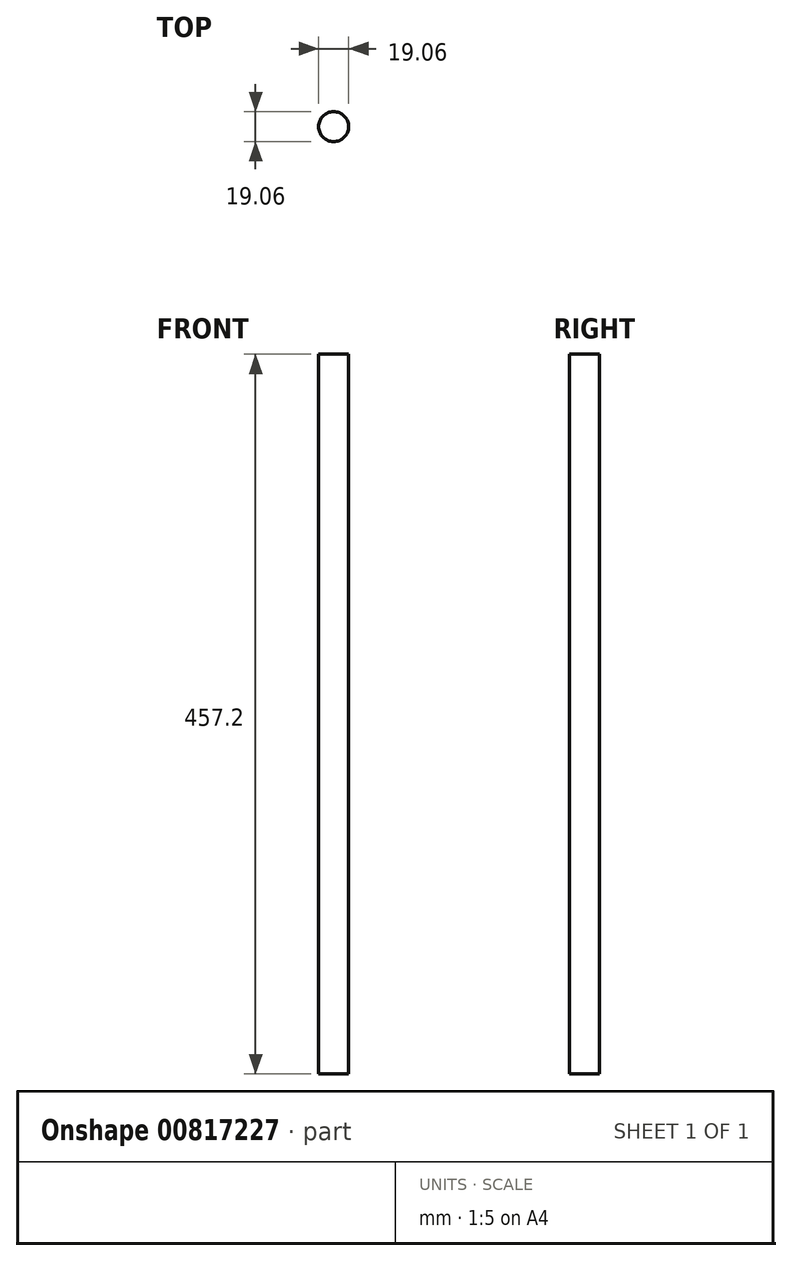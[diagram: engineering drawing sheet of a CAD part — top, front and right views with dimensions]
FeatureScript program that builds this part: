
annotation { "Feature Type Name" : "Feature", "Feature Type Description" : "" }
export const myFeature = defineFeature(function(context is Context, id is Id, definition is map)
    precondition{}
    {
        {
            var Q0;
            Q0=qCreatedBy(makeId("Top.planeOp"),FACE);
            var sketch = newSketch(context, id + "F0", { "sketchPlane" : qUnion([Q0])});
            skCircle(sketch, "E0", {"center": v(0, 0) * mm, "radius": 9.53 * mm});
            skSolve(sketch);
        }
        {
            var Q0;
            Q0=sQuery(id+"F0.wireOp",EDGE,"E0");
            extrude(context, id + "F1", {"bodyType" : ToolBodyType.SURFACE, "surfaceEntities" : qUnion([Q0]), "depth" : 457.2 * mm, "offsetDistance" : 25.4 * mm});
        }
    });
